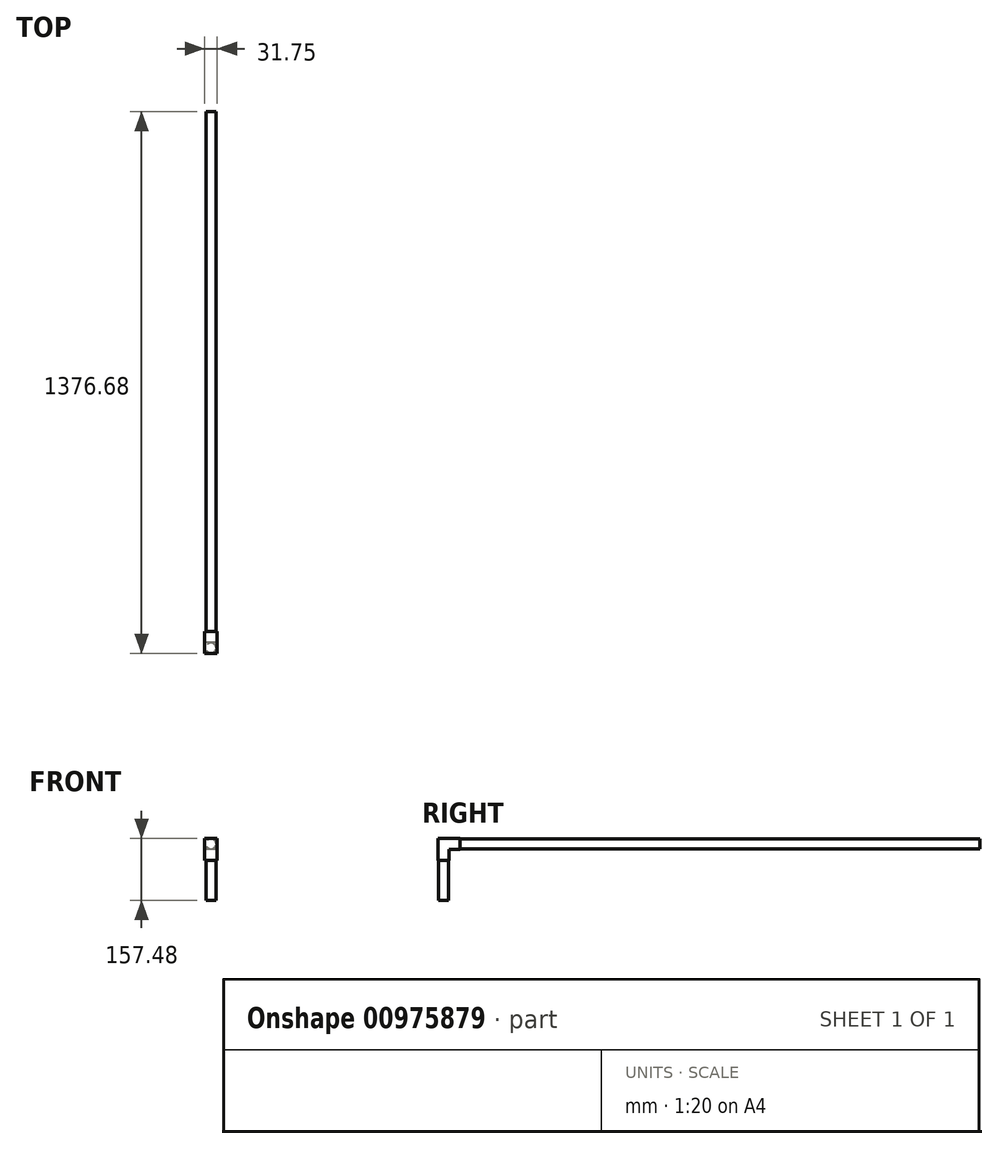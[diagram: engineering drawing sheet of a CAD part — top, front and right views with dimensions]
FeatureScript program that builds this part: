
annotation { "Feature Type Name" : "Feature", "Feature Type Description" : "" }
export const myFeature = defineFeature(function(context is Context, id is Id, definition is map)
    precondition{}
    {
        {
            var Q0;
            Q0=qCreatedBy(makeId("Right.planeOp"),FACE);
            var sketch = newSketch(context, id + "F0", { "sketchPlane" : qUnion([Q0])});
            skLineSegment(sketch, "E0.bottom", {"start": v(-53.67, 56.26) * mm, "end": v(-25.73, 56.26) * mm});
            skLineSegment(sketch, "E0.top", {"start": v(-53.67, 0.38) * mm, "end": v(-25.73, 0.38) * mm});
            skLineSegment(sketch, "E0.left", {"start": v(-53.67, 56.26) * mm, "end": v(-53.67, 0.38) * mm});
            skLineSegment(sketch, "E0.right", {"start": v(-25.73, 28.32) * mm, "end": v(-25.73, 0.38) * mm});
            skLineSegment(sketch, "E1.bottom", {"start": v(-25.73, 56.26) * mm, "end": v(2.2, 56.26) * mm});
            skLineSegment(sketch, "E1.top", {"start": v(-25.73, 28.32) * mm, "end": v(2.2, 28.32) * mm});
            skLineSegment(sketch, "E1.right", {"start": v(2.2, 56.26) * mm, "end": v(2.2, 28.32) * mm});
            skSolve(sketch);
        }
        {
            var Q0;
            Q0=makeQuery(id+"F0.imprint","IMPRINT",FACE,{"disambiguationData":[TD([[makeQuery(id+"F0.imprint","IMPRINT",EDGE,{"derivedFrom":sQuery(id+"F0.wireOp",EDGE,"E0.bottom")}),-1.0]])]});
            extrude(context, id + "F1", {"entities" : qUnion([Q0]), "depth" : 31.75 * mm, "offsetDistance" : 25.4 * mm});
        }
        {
            var Q0;
            Q0=makeQuery(id+"F1.opExtrude","SWEPT_FACE",FACE,{"disambiguationData":[OSD([sQuery(id+"F0.wireOp",EDGE,"E1.right")])]});
            var sketch = newSketch(context, id + "F2", { "sketchPlane" : qUnion([Q0])});
            skCircle(sketch, "E2", {"center": v(-15.88, 42.3) * mm, "radius": 12.7 * mm});
            skPoint(sketch, "E2.centerSnap0", {"position": v(0, 42.3) * mm});
            skPoint(sketch, "E2.centerSnap1", {"position": v(-15.88, 56.26) * mm});
            skSolve(sketch);
        }
        {
            var Q0;
            Q0=makeQuery(id+"F2.imprint","IMPRINT",FACE,{"disambiguationData":[TD([[makeQuery(id+"F2.imprint","IMPRINT",EDGE,{"derivedFrom":sQuery(id+"F2.wireOp",EDGE,"E2")}),1.0]])]});
            extrude(context, id + "F3", {"entities" : qUnion([Q0]), "operationType" : NewBodyOperationType.ADD, "depth" : 1320.8 * mm, "offsetDistance" : 25.4 * mm});
        }
        {
            var Q0;
            Q0=makeQuery(id+"F1.opExtrude","SWEPT_FACE",FACE,{"disambiguationData":[OSD([sQuery(id+"F0.wireOp",EDGE,"E0.top")])]});
            var sketch = newSketch(context, id + "F4", { "sketchPlane" : qUnion([Q0])});
            skCircle(sketch, "E3", {"center": v(15.88, 39.7) * mm, "radius": 12.7 * mm});
            skPoint(sketch, "E3.centerSnap0", {"position": v(0, 39.7) * mm});
            skPoint(sketch, "E3.centerSnap1", {"position": v(15.88, 25.73) * mm});
            skSolve(sketch);
        }
        {
            var Q0;
            Q0=makeQuery(id+"F4.imprint","IMPRINT",FACE,{"disambiguationData":[TD([[makeQuery(id+"F4.imprint","IMPRINT",EDGE,{"derivedFrom":sQuery(id+"F4.wireOp",EDGE,"E3")}),1.0]])]});
            extrude(context, id + "F5", {"entities" : qUnion([Q0]), "operationType" : NewBodyOperationType.ADD, "depth" : 101.6 * mm, "offsetDistance" : 25.4 * mm});
        }
    });
